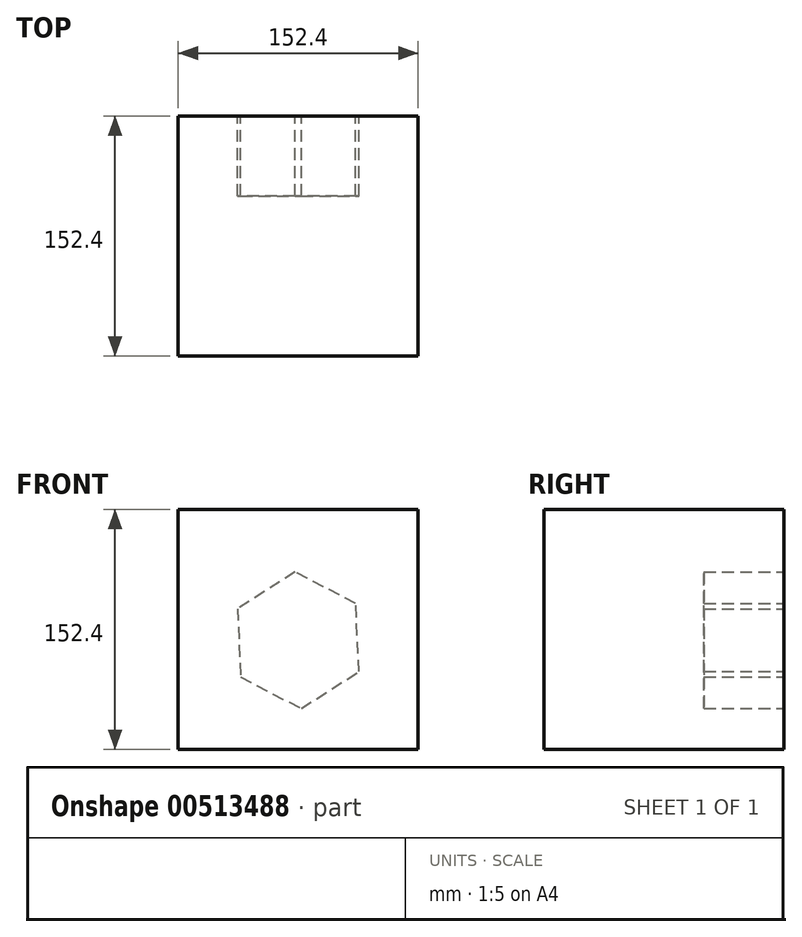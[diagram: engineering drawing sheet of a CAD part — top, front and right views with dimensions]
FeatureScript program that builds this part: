
annotation { "Feature Type Name" : "Feature", "Feature Type Description" : "" }
export const myFeature = defineFeature(function(context is Context, id is Id, definition is map)
    precondition{}
    {
        {
            var Q0;
            Q0=qCreatedBy(makeId("Top.planeOp"),FACE);
            var sketch = newSketch(context, id + "F0", { "sketchPlane" : qUnion([Q0])});
            skLineSegment(sketch, "E0.bottom", {"start": v(76.2, -76.2) * mm, "end": v(-76.2, -76.2) * mm});
            skLineSegment(sketch, "E0.top", {"start": v(76.2, 76.2) * mm, "end": v(-76.2, 76.2) * mm});
            skLineSegment(sketch, "E0.left", {"start": v(76.2, -76.2) * mm, "end": v(76.2, 76.2) * mm});
            skLineSegment(sketch, "E0.right", {"start": v(-76.2, -76.2) * mm, "end": v(-76.2, 76.2) * mm});
            skPoint(sketch, "E0.middle", {"position": v(0, 0) * mm});
            skSolve(sketch);
        }
        {
            var Q0;
            Q0=makeQuery(id+"F0.imprint","IMPRINT",FACE,{"disambiguationData":[TD([[makeQuery(id+"F0.imprint","IMPRINT",EDGE,{"derivedFrom":sQuery(id+"F0.wireOp",EDGE,"E0.bottom")}),-1.0]])]});
            extrude(context, id + "F1", {"entities" : qUnion([Q0]), "depth" : 152.4 * mm});
        }
        {
            var Q0;
            Q0=makeQuery(id+"F1.opExtrude","SWEPT_FACE",FACE,{"disambiguationData":[OSD([sQuery(id+"F0.wireOp",EDGE,"E0.left")])]});
            var sketch = newSketch(context, id + "F2", { "sketchPlane" : qUnion([Q0])});
            skCircle(sketch, "E1", {"center": v(28.55, 63.34) * mm, "radius": 37.42 * mm});
            skSolve(sketch);
        }
        {
            var Q0;
            Q0=sQuery(id+"F2.wireOp",EDGE,"E1");
            extrude(context, id + "F3", {"bodyType" : ToolBodyType.SURFACE, "surfaceEntities" : qUnion([Q0]), "depth" : 25.4 * mm});
        }
        {
            var Q0;
            Q0=makeQuery(id+"F1.opExtrude","SWEPT_FACE",FACE,{"disambiguationData":[OSD([sQuery(id+"F0.wireOp",EDGE,"E0.top")])]});
            var sketch = newSketch(context, id + "F4", { "sketchPlane" : qUnion([Q0])});
            skCircle(sketch, "E2.cCircle", {"center": v(0, 69.35) * mm, "radius": 43.39 * mm, "construction": true});
            skLineSegment(sketch, "E2.0", {"start": v(36.54, 45.95) * mm, "end": v(-2, 26) * mm});
            skLineSegment(sketch, "E2.1", {"start": v(-2, 26) * mm, "end": v(-38.53, 49.4) * mm});
            skLineSegment(sketch, "E2.2", {"start": v(-38.53, 49.4) * mm, "end": v(-36.54, 92.74) * mm});
            skLineSegment(sketch, "E2.3", {"start": v(-36.54, 92.74) * mm, "end": v(2, 112.69) * mm});
            skLineSegment(sketch, "E2.4", {"start": v(2, 112.69) * mm, "end": v(38.53, 89.3) * mm});
            skLineSegment(sketch, "E2.5", {"start": v(38.53, 89.3) * mm, "end": v(36.54, 45.95) * mm});
            skSolve(sketch);
        }
        {
            var Q0;
            Q0=makeQuery(id+"F4.imprint","IMPRINT",FACE,{"disambiguationData":[TD([[makeQuery(id+"F4.imprint","IMPRINT",EDGE,{"derivedFrom":sQuery(id+"F4.wireOp",EDGE,"E2.0")}),-1.0]])]});
            extrude(context, id + "F5", {"entities" : qUnion([Q0]), "operationType" : NewBodyOperationType.REMOVE, "oppositeDirection" : true, "depth" : 50.8 * mm});
        }
    });
